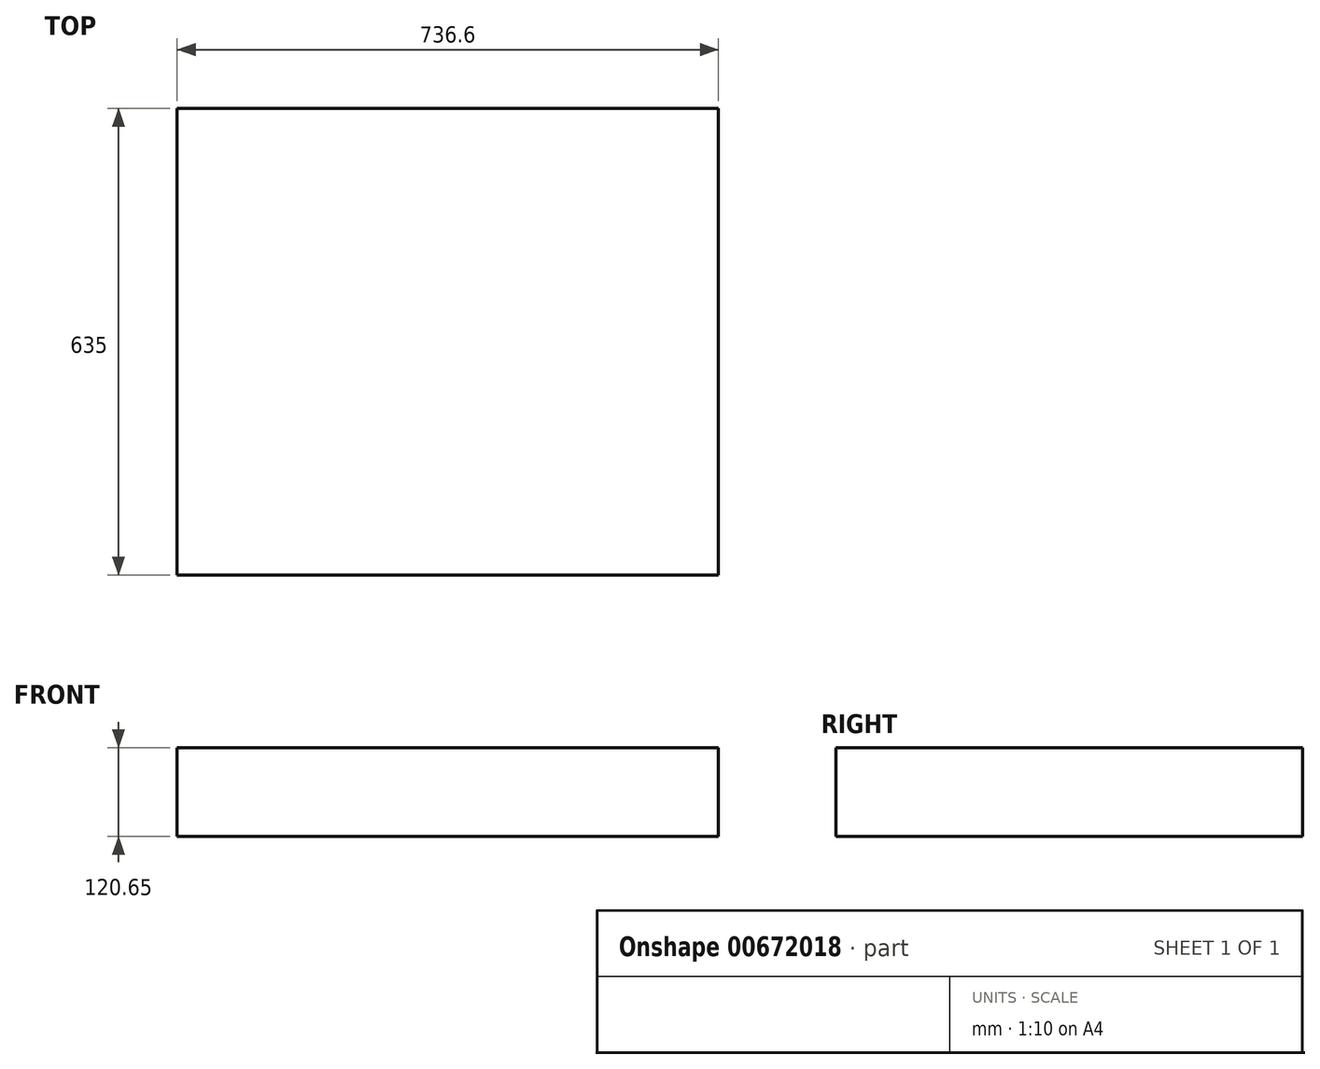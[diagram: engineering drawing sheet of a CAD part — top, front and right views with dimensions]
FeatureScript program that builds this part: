
annotation { "Feature Type Name" : "Feature", "Feature Type Description" : "" }
export const myFeature = defineFeature(function(context is Context, id is Id, definition is map)
    precondition{}
    {
        {
            var Q0;
            Q0=qCreatedBy(makeId("Top.planeOp"),FACE);
            var sketch = newSketch(context, id + "F0", { "sketchPlane" : qUnion([Q0])});
            skLineSegment(sketch, "E0.bottom", {"start": v(368.3, -317.5) * mm, "end": v(-368.3, -317.5) * mm});
            skLineSegment(sketch, "E0.top", {"start": v(368.3, 317.5) * mm, "end": v(-368.3, 317.5) * mm});
            skLineSegment(sketch, "E0.left", {"start": v(368.3, -317.5) * mm, "end": v(368.3, 317.5) * mm});
            skLineSegment(sketch, "E0.right", {"start": v(-368.3, -317.5) * mm, "end": v(-368.3, 317.5) * mm});
            skPoint(sketch, "E0.middle", {"position": v(0, 0) * mm});
            skSolve(sketch);
        }
        {
            var Q0;
            Q0 = qSketchRegion(id + "F0", true);
            extrude(context, id + "F1", {"entities" : qUnion([Q0]), "oppositeDirection" : true, "depth" : 120.65 * mm, "offsetDistance" : 25.4 * mm});
        }
    });
